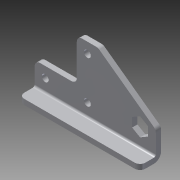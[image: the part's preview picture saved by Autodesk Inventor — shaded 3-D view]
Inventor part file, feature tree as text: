
AUTODESK INVENTOR PART (.ipt)
format: ipt  version: 2014 (Build 180170000, 170)  size: 138,752 bytes
history: native  units: in
note: dims shown in document units (in); Inventor stores cm internally (conversion verified against a paired STEP export)
features: sheet_metal_op x4, sketch x2, other x2, fillet x1
ambient origin geometry x8: Origin, YZ Plane, XZ Plane, XY Plane, X Axis, Y Axis, Z Axis, Center Point
bodies: Solid1 (feature_tree)
feature tree (9):
  sheet_metal_op  "Face1"
  sheet_metal_op  "Flange1"
  fillet  "Fillet2"  Radius=0.5in
  sketch  "Sketch1"  dims[d1=1.0in]
  other  "Plate1"
  sketch  "Sketch2"  dims[d2=1.0in d3=0.5in d4=2.875in d5=0.375in d6=0.375in d7=0.375in d8=90.0deg d9=0.5in d10=0.163in d11=0.25in d12=0.25in d13=0.7874in d15=1.0in d16=0.3937in d18=1.0in d20=0.7874in d22=1.0in d23=0.3937in d25=1.0in d27=0.125in d29=0.125in d30=0.0625in d31=0.25in d32=0.125in d33=0.5in d34=90.0deg d35=0.05in d36=0.5in d37=0.125in d38=0.125in d39=0.125in]
  other  "Plate2"
  sheet_metal_op  "Bend1"
  sheet_metal_op  "Corner1"
